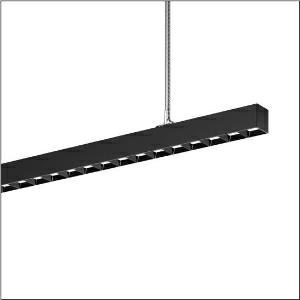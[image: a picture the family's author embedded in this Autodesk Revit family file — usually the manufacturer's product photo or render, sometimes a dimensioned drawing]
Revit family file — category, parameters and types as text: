
# Revit family: silica_r__21_51mx34dc4dbb_b20b
name_source: partatom
category: Lighting Fixtures
units: mm (PartAtom-declared; Revit-internal decimal feet)

## family parameters
Cut with Voids When Loaded = No
Host = Face
Light Source = No
Part Type = Normal
Room Calculation Point = No
Round Connector Dimension = Use Diameter
Shared = No

## types (1)
- --- (1 x LED, 19200 lm, 120.3 W, 4000K)
    Apparent Load = 120 VA
    CIE Flux Codes = 74 94 99 56 100
    Color Rendering = 80
    Color Temperature = 4000K
    Default Elevation = 1800 mm
    Description = Silica® 21, office luminaire, primary light control with darklight reflector, of PMMA, black, light emission: direct/indirect distribution, primary light characteristic: asymmetric, installation type: suspended mounting, LED, rated luminous flux: 19.200lm, luminous efficacy: 160lm/W, light colour: 840, colour temperature: 4000K, with terminal, 3+2-pole, max. 2.5mm², mains connection: 220..240V, AC, 50/60Hz, rated input power: 120.3W, luminaire housing, of aluminium, jet black (RAL 9005), length: 3.004mm, width: 53mm, height: 53mm, protection rating (complete): IP20, insulation class (complete): insulation class I (protective earthing), certification: CE, permissible operating ambient temperature: 0..+35°C, standard: EN 50419, packaging unit: 1 piece
    Height = 53 mm
    Lamp = 1 x LED
    Lamp Light Flux = 19200 lm
    Lamp Power = 120.3 W
    Lamp count = 1
    Length = 3004 mm
    Luminous efficacy = 160 lm/W
    Manufacturer = Siteco
    ModVariant = No
    Model = 51MX34DC4DBB
    Mounting Place = Ceiling
    Mounting Type = Pendant
    Number of Poles = 1
    OnlyDefault = Yes
    Power Factor = 1
    Product Name = Silica® 21
    Product group = office luminaire | ceiling pendant
    ProductGroupID = 902
    Protection Class = Protection class I
    Protection Degree = IP 20
    RLX_Detail_Level = 1
    RLX_Emergency_Light_Flux = 0 lm
    RLX_Emergency_Type = 0
    RLX_Emergency_Type_DB = No
    RlxData = <blob elided: 68629 chars, md5=42e12d19>
    Socket = socket
    Standby Power = 0 W
    System Light Flux = 19200 lm
    System Power = 120 W
    Type Comments = factory setting: luminous flux: 100 % | dim-lin: 254 | 418 mA
    Type Image = l_1297774.jpg
    URL = http://relux.com
    VarID = @adj_050789
    Voltage = 0 V
    Weight = 0.00 kg
    Width = 53 mm

## geometry (parser evidence)
native form markers: Blend x4, Sweep x11
no freeform markers — native parametric forms only
